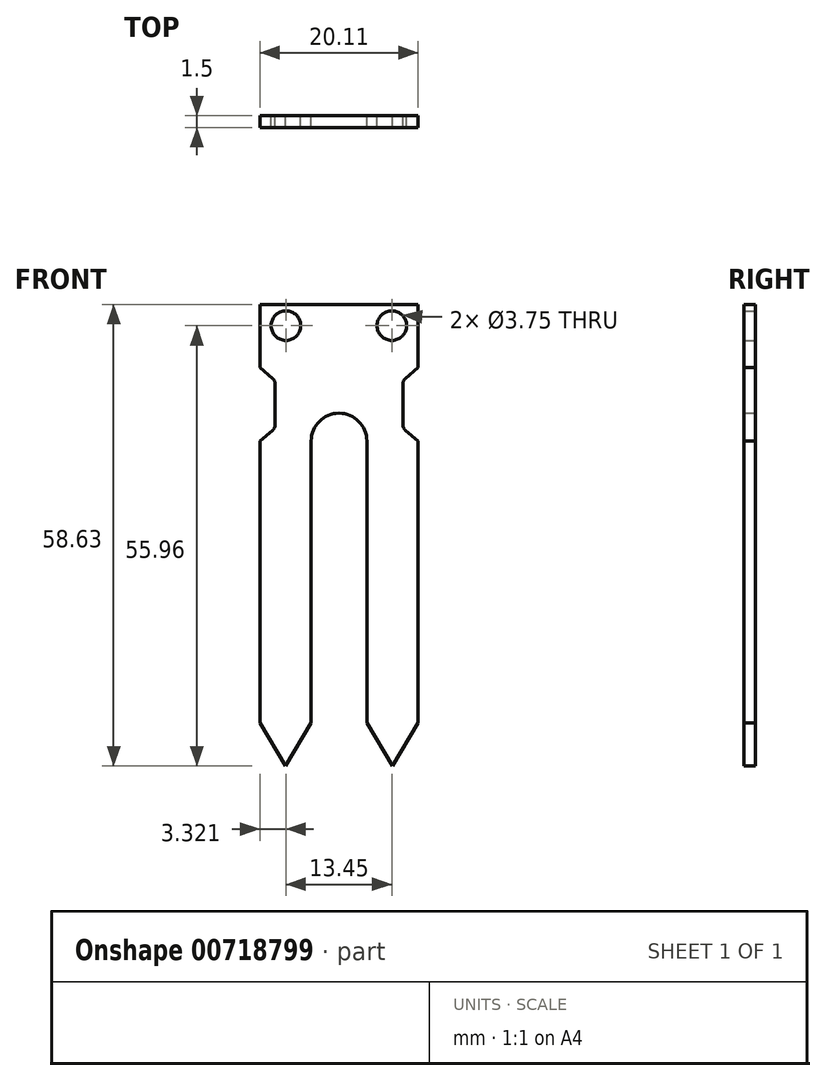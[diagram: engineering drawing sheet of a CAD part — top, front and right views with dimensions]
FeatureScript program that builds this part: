
annotation { "Feature Type Name" : "Feature", "Feature Type Description" : "" }
export const myFeature = defineFeature(function(context is Context, id is Id, definition is map)
    precondition{}
    {
        {
            var Q0;
            Q0=qCreatedBy(makeId("Front.planeOp"),FACE);
            var sketch = newSketch(context, id + "F0", { "sketchPlane" : qUnion([Q0])});
            skLineSegment(sketch, "E0", {"start": v(-10.05, 0) * mm, "end": v(10.05, 0) * mm});
            skLineSegment(sketch, "E1", {"start": v(10.05, -17.33) * mm, "end": v(10.06, -53.17) * mm});
            skLineSegment(sketch, "E2", {"start": v(-10.06, -17.33) * mm, "end": v(-10.06, -53.17) * mm});
            skLineSegment(sketch, "E3", {"start": v(-10.05, -53.17) * mm, "end": v(-6.8, -58.63) * mm});
            skLineSegment(sketch, "E4", {"start": v(-6.8, -58.63) * mm, "end": v(-3.54, -53.17) * mm});
            skLineSegment(sketch, "E5", {"start": v(-3.54, -53.17) * mm, "end": v(-3.54, -17.33) * mm});
            skLineSegment(sketch, "E6", {"start": v(3.54, -53.17) * mm, "end": v(3.54, -17.33) * mm});
            skLineSegment(sketch, "E7", {"start": v(3.54, -53.17) * mm, "end": v(6.8, -58.63) * mm});
            skLineSegment(sketch, "E8", {"start": v(6.8, -58.63) * mm, "end": v(10.06, -53.17) * mm});
            skArc(sketch, "E9", {"start": v(3.54, -17.33) * mm, "mid": v(0, -13.79) * mm, "end": v(-3.54, -17.33) * mm});
            skLineSegment(sketch, "E10", {"start": v(-10.06, -8) * mm, "end": v(-8.1, -9.66) * mm});
            skLineSegment(sketch, "E11", {"start": v(-8.1, -9.66) * mm, "end": v(-8.1, -15.66) * mm});
            skLineSegment(sketch, "E12", {"start": v(-10.05, -17.33) * mm, "end": v(-8.1, -15.66) * mm});
            skLineSegment(sketch, "E13", {"start": v(10.05, -8) * mm, "end": v(8.1, -9.66) * mm});
            skLineSegment(sketch, "E14", {"start": v(8.1, -9.66) * mm, "end": v(8.1, -15.66) * mm});
            skLineSegment(sketch, "E15", {"start": v(8.1, -15.66) * mm, "end": v(10.06, -17.33) * mm});
            skLineSegment(sketch, "E16", {"start": v(-10.05, -2.6) * mm, "end": v(-8.87, -2.6) * mm, "construction": true});
            skLineSegment(sketch, "E17", {"start": v(10.05, -2.6) * mm, "end": v(8.87, -2.6) * mm, "construction": true});
            skCircle(sketch, "E18", {"center": v(-6.74, -2.67) * mm, "radius": 1.88 * mm});
            skCircle(sketch, "E19", {"center": v(6.71, -2.67) * mm, "radius": 1.88 * mm});
            skPoint(sketch, "E20", {"position": v(0, -13.79) * mm});
            skLineSegment(sketch, "E21", {"start": v(-10.05, 0) * mm, "end": v(-10.06, -8) * mm});
            skLineSegment(sketch, "E22", {"start": v(10.05, 0) * mm, "end": v(10.05, -8) * mm});
            skSolve(sketch);
        }
        {
            var Q0;
            Q0=makeQuery(id+"F0.imprint","IMPRINT",FACE,{"disambiguationData":[TD([[makeQuery(id+"F0.imprint","IMPRINT",EDGE,{"derivedFrom":sQuery(id+"F0.wireOp",EDGE,"E0")}),-1.0]])]});
            extrude(context, id + "F1", {"entities" : qUnion([Q0]), "depth" : 1.5 * mm, "offsetDistance" : 25 * mm});
        }
        {
            var Q0;
            Q0=makeQuery(id+"F1.opExtrude","SWEPT_EDGE",EDGE,{"disambiguationData":[OSD([sQuery(id+"F0.wireOp",EDGE,"E10"),sQuery(id+"F0.wireOp",EDGE,"E11")])]});
            var Q1;
            Q1=makeQuery(id+"F1.opExtrude","SWEPT_EDGE",EDGE,{"disambiguationData":[OSD([sQuery(id+"F0.wireOp",EDGE,"E11"),sQuery(id+"F0.wireOp",EDGE,"E12")])]});
            var Q2;
            Q2=makeQuery(id+"F1.opExtrude","SWEPT_EDGE",EDGE,{"disambiguationData":[OSD([sQuery(id+"F0.wireOp",EDGE,"E13"),sQuery(id+"F0.wireOp",EDGE,"E14")])]});
            var Q3;
            Q3=makeQuery(id+"F1.opExtrude","SWEPT_EDGE",EDGE,{"disambiguationData":[OSD([sQuery(id+"F0.wireOp",EDGE,"E14"),sQuery(id+"F0.wireOp",EDGE,"E15")])]});
            fillet(context, id + "F2", {"entities" : qUnion([Q0, Q1, Q2, Q3]), "radius" : 1 * mm, "tangentPropagation" : true, "allowEdgeOverflow" : false});
        }
    });
